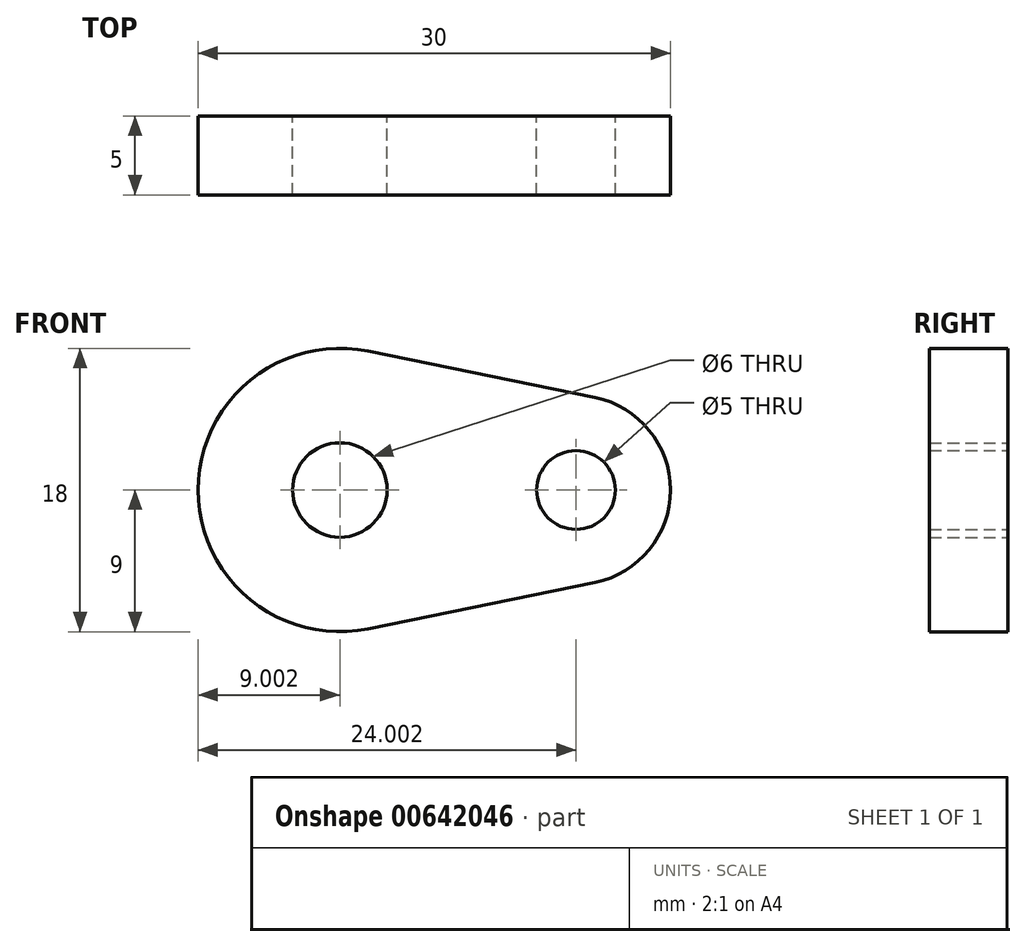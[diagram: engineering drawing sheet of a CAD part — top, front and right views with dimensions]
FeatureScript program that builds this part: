
annotation { "Feature Type Name" : "Feature", "Feature Type Description" : "" }
export const myFeature = defineFeature(function(context is Context, id is Id, definition is map)
    precondition{}
    {
        {
            var Q0;
            Q0=qCreatedBy(makeId("Front.planeOp"),FACE);
            var sketch = newSketch(context, id + "F0", { "sketchPlane" : qUnion([Q0])});
            skCircle(sketch, "E0", {"center": v(-28.06, 0) * mm, "radius": 3 * mm});
            skCircle(sketch, "E1", {"center": v(-13.06, 0) * mm, "radius": 2.5 * mm});
            skArc(sketch, "E2", {"start": v(-26.26, 8.82) * mm, "mid": v(-37.06, 0) * mm, "end": v(-26.26, -8.82) * mm});
            skArc(sketch, "E3", {"start": v(-11.86, -5.88) * mm, "mid": v(-7.06, 0) * mm, "end": v(-11.86, 5.88) * mm});
            skLineSegment(sketch, "E4", {"start": v(-26.26, 8.82) * mm, "end": v(-11.86, 5.88) * mm});
            skLineSegment(sketch, "E5", {"start": v(-26.26, -8.82) * mm, "end": v(-11.86, -5.88) * mm});
            skSolve(sketch);
        }
        {
            var Q0;
            Q0=makeQuery(id+"F0.imprint","IMPRINT",FACE,{"disambiguationData":[TD([[makeQuery(id+"F0.imprint","IMPRINT",EDGE,{"derivedFrom":sQuery(id+"F0.wireOp",EDGE,"E0")}),-1.0]])]});
            extrude(context, id + "F1", {"entities" : qUnion([Q0]), "depth" : 5 * mm, "offsetDistance" : 25 * mm});
        }
    });
